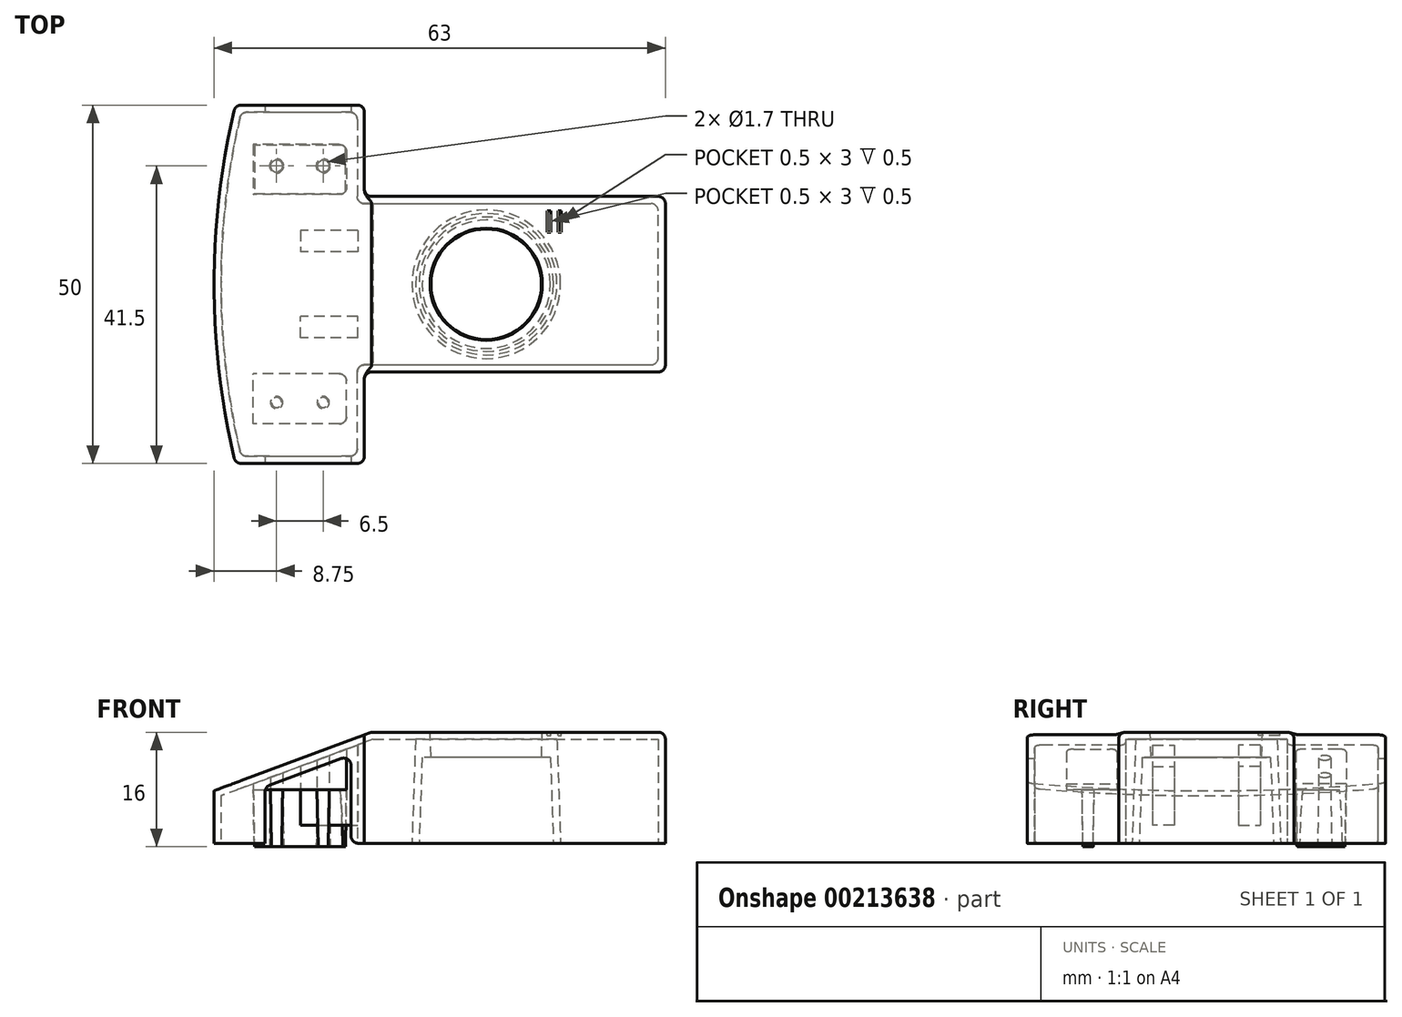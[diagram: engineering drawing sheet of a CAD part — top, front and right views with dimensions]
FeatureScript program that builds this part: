
annotation { "Feature Type Name" : "Feature", "Feature Type Description" : "" }
export const myFeature = defineFeature(function(context is Context, id is Id, definition is map)
    precondition{}
    {
        {
            var Q0;
            Q0=qCreatedBy(makeId("Top.planeOp"),FACE);
            var sketch = newSketch(context, id + "F0", { "sketchPlane" : qUnion([Q0])});
            skCircle(sketch, "E0", {"center": v(-4, 0) * mm, "radius": 9.37 * mm});
            skLineSegment(sketch, "E1.bottom", {"start": v(-21, -12.25) * mm, "end": v(21, -12.25) * mm});
            skLineSegment(sketch, "E1.top", {"start": v(-21, 12.25) * mm, "end": v(21, 12.25) * mm});
            skLineSegment(sketch, "E1.right", {"start": v(21, -12.25) * mm, "end": v(21, 12.25) * mm});
            skLineSegment(sketch, "E2.bottom", {"start": v(-21, -25) * mm, "end": v(-39, -25) * mm});
            skLineSegment(sketch, "E2.top", {"start": v(-21, 25) * mm, "end": v(-39, 25) * mm});
            skLineSegment(sketch, "E2.left", {"start": v(-21, -25) * mm, "end": v(-21, -12.25) * mm});
            skLineSegment(sketch, "E2.right", {"start": v(-39, -25) * mm, "end": v(-39, 25) * mm});
            skPoint(sketch, "E2.middle", {"position": v(-30, 0) * mm});
            skLineSegment(sketch, "E3.trimOffspring", {"start": v(-21, 12.25) * mm, "end": v(-21, 25) * mm});
            skLineSegment(sketch, "E4", {"start": v(-20, 12.25) * mm, "end": v(-20, -12.25) * mm});
            skPoint(sketch, "E5", {"position": v(-42, 0) * mm});
            skPoint(sketch, "E5.positionSnap0", {"position": v(-39, 0) * mm});
            skArc(sketch, "E6", {"start": v(-39, 25) * mm, "mid": v(-42, 0) * mm, "end": v(-39, -25) * mm});
            skSolve(sketch);
        }
        {
            var Q0;
            Q0=qSketchRegion(id+"F0",true);
            var Q1;
            Q1=makeQuery(id+"F0.imprint","IMPRINT",FACE,{"disambiguationData":[TD([[makeQuery(id+"F0.imprint","IMPRINT",EDGE,{"derivedFrom":sQuery(id+"F0.wireOp",EDGE,"E0")}),1.0]])]});
            extrude(context, id + "F1", {"entities" : qUnion([Q0, Q1]), "depth" : 15.5 * mm});
        }
        {
            var Q0;
            Q0=makeQuery(id+"F0.imprint","IMPRINT",FACE,{"disambiguationData":[TD([[makeQuery(id+"F0.imprint","IMPRINT",EDGE,{"derivedFrom":sQuery(id+"F0.wireOp",EDGE,"E0")}),1.0]])]});
            var Q1;
            Q1=makeQuery(id+"F1.opExtrude","CAP_FACE",FACE,{"disambiguationData":[OSD([sQuery(id+"F0.wireOp",EDGE,"E1.bottom"),sQuery(id+"F0.wireOp",EDGE,"E1.top"),sQuery(id+"F0.wireOp",EDGE,"E1.right"),sQuery(id+"F0.wireOp",EDGE,"E2.bottom"),sQuery(id+"F0.wireOp",EDGE,"E2.top"),sQuery(id+"F0.wireOp",EDGE,"E2.left"),sQuery(id+"F0.wireOp",EDGE,"E3.trimOffspring"),sQuery(id+"F0.wireOp",EDGE,"E6")])],"isStart":false});
            extrude(context, id + "F2", {"entities" : qUnion([Q0]), "operationType" : NewBodyOperationType.REMOVE, "endBound" : BoundingType.UP_TO_SURFACE, "endBoundEntityFace" : qUnion([Q1]), "depth" : 25 * mm, "hasDraft" : true, "draftAngle" : 2 * degree, "draftPullDirection" : true});
        }
        {
            var Q0;
            Q0=qCreatedBy(makeId("Front.planeOp"),FACE);
            var Q1;
            Q1=makeQuery(id+"F1.opExtrude","CAP_EDGE",EDGE,{"disambiguationData":[OSD([sQuery(id+"F0.wireOp",EDGE,"E2.bottom")])],"isStart":true});
            cPlane(context, id + "F3", {"entities" : qUnion([Q0, Q1]), "cplaneType" : CPlaneType.LINE_ANGLE, "offset" : 25 * mm, "angle" : 0 * degree, "width" : 150 * mm, "height" : 150 * mm});
        }
        {
            var Q0;
            Q0=qCreatedBy(id+"F3.planeOp",FACE);
            var sketch = newSketch(context, id + "F4", { "sketchPlane" : qUnion([Q0])});
            skLineSegment(sketch, "E7", {"start": v(20, 15.5) * mm, "end": v(42, 15.5) * mm});
            skLineSegment(sketch, "E8", {"start": v(42, 15.5) * mm, "end": v(42, 7.32) * mm});
            skLineSegment(sketch, "E9", {"start": v(42, 7.32) * mm, "end": v(20, 15.5) * mm});
            skLineSegment(sketch, "E10", {"start": v(42, 0) * mm, "end": v(41.46, 15.5) * mm, "construction": true});
            skLineSegment(sketch, "E11", {"start": v(42, 0) * mm, "end": v(42, 27.73) * mm, "construction": true});
            skSolve(sketch);
        }
        {
            var Q0;
            Q0=qSketchRegion(id+"F4",true);
            extrude(context, id + "F5", {"entities" : qUnion([Q0]), "operationType" : NewBodyOperationType.REMOVE, "endBound" : BoundingType.THROUGH_ALL, "depth" : 25 * mm});
        }
        {
            var Q0;
            Q0=makeQuery(id+"F1.opExtrude","CAP_FACE",FACE,{"disambiguationData":[OSD([sQuery(id+"F0.wireOp",EDGE,"E1.bottom"),sQuery(id+"F0.wireOp",EDGE,"E1.top"),sQuery(id+"F0.wireOp",EDGE,"E1.right"),sQuery(id+"F0.wireOp",EDGE,"E2.bottom"),sQuery(id+"F0.wireOp",EDGE,"E2.top"),sQuery(id+"F0.wireOp",EDGE,"E2.left"),sQuery(id+"F0.wireOp",EDGE,"E3.trimOffspring"),sQuery(id+"F0.wireOp",EDGE,"E6")])],"isStart":true});
            shell(context, id + "F6", {"entities" : qUnion([Q0]), "thickness" : 1 * mm});
        }
        {
            var Q0;
            Q0=makeQuery(id+"F1.opExtrude","SWEPT_FACE",FACE,{"disambiguationData":[OSD([sQuery(id+"F0.wireOp",EDGE,"E2.bottom")])]});
            var sketch = newSketch(context, id + "F7", { "sketchPlane" : qUnion([Q0])});
            skLineSegment(sketch, "E12", {"start": v(-20, 15.5) * mm, "end": v(-39, 8.43) * mm});
            skLineSegment(sketch, "E13", {"start": v(-39, 8.43) * mm, "end": v(-39, 15.5) * mm});
            skLineSegment(sketch, "E14", {"start": v(-39, 15.5) * mm, "end": v(-20, 15.5) * mm});
            skLineSegment(sketch, "E15", {"start": v(-34.87, 0) * mm, "end": v(-34.87, 7.86) * mm});
            skLineSegment(sketch, "E16", {"start": v(-34.87, 7.86) * mm, "end": v(-22.87, 12.32) * mm});
            skLineSegment(sketch, "E17", {"start": v(-22.87, 0) * mm, "end": v(-34.87, 0) * mm});
            skLineSegment(sketch, "E18", {"start": v(-22.87, 12.32) * mm, "end": v(-22.87, 0) * mm});
            skSolve(sketch);
        }
        {
            var Q0;
            Q0=makeQuery(id+"F7.imprint","IMPRINT",FACE,{"disambiguationData":[TD([[makeQuery(id+"F7.imprint","IMPRINT",EDGE,{"derivedFrom":sQuery(id+"F7.wireOp",EDGE,"E15")}),-1.0]])]});
            extrude(context, id + "F8", {"entities" : qUnion([Q0]), "operationType" : NewBodyOperationType.REMOVE, "endBound" : BoundingType.THROUGH_ALL, "oppositeDirection" : true, "depth" : 25 * mm});
        }
        {
            var Q0;
            Q0=makeQuery(id+"F1.opExtrude","CAP_FACE",FACE,{"disambiguationData":[OSD([sQuery(id+"F0.wireOp",EDGE,"E0"),sQuery(id+"F0.wireOp",EDGE,"E1.bottom"),sQuery(id+"F0.wireOp",EDGE,"E1.top"),sQuery(id+"F0.wireOp",EDGE,"E1.right"),sQuery(id+"F0.wireOp",EDGE,"E2.bottom"),sQuery(id+"F0.wireOp",EDGE,"E2.top"),sQuery(id+"F0.wireOp",EDGE,"E2.left"),sQuery(id+"F0.wireOp",EDGE,"E2.right"),sQuery(id+"F0.wireOp",EDGE,"E3.trimOffspring")])],"isStart":false});
            cPlane(context, id + "F9", {"entities" : qUnion([Q0]), "cplaneType" : CPlaneType.OFFSET, "offset" : 8 * mm, "oppositeDirection" : true, "width" : 150 * mm, "height" : 150 * mm});
        }
        {
            var Q0;
            Q0=qCreatedBy(id+"F9.planeOp",FACE);
            var sketch = newSketch(context, id + "F10", { "sketchPlane" : qUnion([Q0])});
            skLineSegment(sketch, "E19", {"start": v(0, 0) * mm, "end": v(-63, 0) * mm, "construction": true});
            skLineSegment(sketch, "E20.bottom", {"start": v(-36.5, -12.5) * mm, "end": v(-23.5, -12.5) * mm});
            skLineSegment(sketch, "E20.top", {"start": v(-36.5, -19.5) * mm, "end": v(-23.5, -19.5) * mm});
            skLineSegment(sketch, "E20.left", {"start": v(-36.5, -12.5) * mm, "end": v(-36.5, -19.5) * mm});
            skLineSegment(sketch, "E20.right", {"start": v(-23.5, -12.5) * mm, "end": v(-23.5, -19.5) * mm});
            skPoint(sketch, "E20.middle", {"position": v(-30, -16) * mm});
            skPoint(sketch, "E21", {"position": v(-33.25, -16.5) * mm});
            skPoint(sketch, "E22", {"position": v(-26.75, -16.5) * mm});
            skCircle(sketch, "E23", {"center": v(-33.25, -16.5) * mm, "radius": 0.85 * mm});
            skCircle(sketch, "E24", {"center": v(-26.75, -16.5) * mm, "radius": 0.85 * mm});
            skLineSegment(sketch, "E25.MirrorCS", {"start": v(-36.5, 12.5) * mm, "end": v(-23.5, 12.5) * mm});
            skLineSegment(sketch, "E26.MirrorCS", {"start": v(-36.5, 12.5) * mm, "end": v(-36.5, 19.5) * mm});
            skLineSegment(sketch, "E27.MirrorCS", {"start": v(-36.5, 19.5) * mm, "end": v(-23.5, 19.5) * mm});
            skLineSegment(sketch, "E28.MirrorCS", {"start": v(-23.5, 12.5) * mm, "end": v(-23.5, 19.5) * mm});
            skCircle(sketch, "E29.MirrorC", {"center": v(-26.75, 16.5) * mm, "radius": 0.85 * mm});
            skCircle(sketch, "E30.MirrorC", {"center": v(-33.25, 16.5) * mm, "radius": 0.85 * mm});
            skSolve(sketch);
        }
        {
            var Q0;
            Q0=makeQuery(id+"F10.imprint","IMPRINT",FACE,{"disambiguationData":[TD([[makeQuery(id+"F10.imprint","IMPRINT",EDGE,{"derivedFrom":sQuery(id+"F10.wireOp",EDGE,"E20.bottom")}),-1.0]])]});
            var Q1;
            Q1=makeQuery(id+"F10.imprint","IMPRINT",FACE,{"disambiguationData":[TD([[makeQuery(id+"F10.imprint","IMPRINT",EDGE,{"derivedFrom":sQuery(id+"F10.wireOp",EDGE,"E23")}),1.0]])]});
            var Q2;
            Q2=makeQuery(id+"F10.imprint","IMPRINT",FACE,{"disambiguationData":[TD([[makeQuery(id+"F10.imprint","IMPRINT",EDGE,{"derivedFrom":sQuery(id+"F10.wireOp",EDGE,"E24")}),1.0]])]});
            var Q3;
            Q3=makeQuery(id+"F10.imprint","IMPRINT",FACE,{"disambiguationData":[TD([[makeQuery(id+"F10.imprint","IMPRINT",EDGE,{"derivedFrom":sQuery(id+"F10.wireOp",EDGE,"E25.MirrorCS")}),1.0]])]});
            var Q4;
            Q4=makeQuery(id+"F10.imprint","IMPRINT",FACE,{"disambiguationData":[TD([[makeQuery(id+"F10.imprint","IMPRINT",EDGE,{"derivedFrom":sQuery(id+"F10.wireOp",EDGE,"E30.MirrorC")}),-1.0]])]});
            var Q5;
            Q5=makeQuery(id+"F10.imprint","IMPRINT",FACE,{"disambiguationData":[TD([[makeQuery(id+"F10.imprint","IMPRINT",EDGE,{"derivedFrom":sQuery(id+"F10.wireOp",EDGE,"E29.MirrorC")}),-1.0]])]});
            var Q6;
            Q6=makeQuery(id+"F6.opShell","OFFSET_FACE",FACE,{"disambiguationData":[OSD([sQuery(id+"F4.wireOp",EDGE,"E9")])]});
            extrude(context, id + "F11", {"entities" : qUnion([Q0, Q1, Q2, Q3, Q4, Q5]), "operationType" : NewBodyOperationType.ADD, "endBound" : BoundingType.UP_TO_SURFACE, "endBoundEntityFace" : qUnion([Q6]), "depth" : 25 * mm});
        }
        {
            var Q0;
            Q0=makeQuery(id+"F10.imprint","IMPRINT",FACE,{"disambiguationData":[TD([[makeQuery(id+"F10.imprint","IMPRINT",EDGE,{"derivedFrom":sQuery(id+"F10.wireOp",EDGE,"E23")}),1.0]])]});
            var Q1;
            Q1=makeQuery(id+"F10.imprint","IMPRINT",FACE,{"disambiguationData":[TD([[makeQuery(id+"F10.imprint","IMPRINT",EDGE,{"derivedFrom":sQuery(id+"F10.wireOp",EDGE,"E29.MirrorC")}),-1.0]])]});
            var Q2;
            Q2=makeQuery(id+"F10.imprint","IMPRINT",FACE,{"disambiguationData":[TD([[makeQuery(id+"F10.imprint","IMPRINT",EDGE,{"derivedFrom":sQuery(id+"F10.wireOp",EDGE,"E30.MirrorC")}),-1.0]])]});
            var Q3;
            Q3=makeQuery(id+"F10.imprint","IMPRINT",FACE,{"disambiguationData":[TD([[makeQuery(id+"F10.imprint","IMPRINT",EDGE,{"derivedFrom":sQuery(id+"F10.wireOp",EDGE,"E24")}),1.0]])]});
            extrude(context, id + "F12", {"entities" : qUnion([Q0, Q1, Q2, Q3]), "operationType" : NewBodyOperationType.ADD, "oppositeDirection" : true, "depth" : 8 * mm, "hasDraft" : true, "draftAngle" : 1 * degree, "draftPullDirection" : true});
        }
        {
            var Q0;
            Q0=makeQuery(id+"F1.opExtrude","CAP_EDGE",EDGE,{"disambiguationData":[OSD([sQuery(id+"F0.wireOp",EDGE,"E1.bottom")])],"isStart":false});
            var Q1;
            Q1=makeQuery(id+"F1.opExtrude","CAP_EDGE",EDGE,{"disambiguationData":[OSD([sQuery(id+"F0.wireOp",EDGE,"E1.right")])],"isStart":false});
            var Q2;
            Q2=makeQuery(id+"F1.opExtrude","CAP_EDGE",EDGE,{"disambiguationData":[OSD([sQuery(id+"F0.wireOp",EDGE,"E1.top")])],"isStart":false});
            var Q3;
            Q3=makeQuery(id+"F1.opExtrude","SWEPT_EDGE",EDGE,{"disambiguationData":[OSD([sQuery(id+"F0.wireOp",EDGE,"E1.bottom"),sQuery(id+"F0.wireOp",EDGE,"E1.right")])]});
            var Q4;
            Q4=makeQuery(id+"F1.opExtrude","SWEPT_EDGE",EDGE,{"disambiguationData":[OSD([sQuery(id+"F0.wireOp",EDGE,"E1.top"),sQuery(id+"F0.wireOp",EDGE,"E1.right")])]});
            fillet(context, id + "F13", {"entities" : qUnion([Q0, Q1, Q2, Q3, Q4]), "radius" : 1 * mm, "tangentPropagation" : true, "allowEdgeOverflow" : false});
        }
        {
            var Q0;
            Q0=makeQuery(id+"F1.opExtrude","SWEPT_EDGE",EDGE,{"disambiguationData":[OSD([sQuery(id+"F0.wireOp",EDGE,"E2.bottom"),sQuery(id+"F0.wireOp",EDGE,"E2.left")])]});
            var Q1;
            Q1=makeQuery(id+"F5.boolean.opBoolean","INTERSECT",EDGE,{"derivedFrom":[makeQuery(id+"F1.opExtrude","SWEPT_FACE",FACE,{"disambiguationData":[OSD([sQuery(id+"F0.wireOp",EDGE,"E2.left")])]}),makeQuery(id+"F5.opExtrude","SWEPT_FACE",FACE,{"disambiguationData":[OSD([sQuery(id+"FjstzwEYRuGCUyq_1.wireOp",EDGE,"6156deb2-2619-4c56-9df6-34b3699534c4")])]})]});
            var Q2;
            Q2=makeQuery(id+"F5.boolean.opBoolean","COPY",EDGE,{"derivedFrom":makeQuery(id+"F5.opExtrude","CAP_EDGE",EDGE,{"disambiguationData":[OSD([sQuery(id+"FjstzwEYRuGCUyq_1.wireOp",EDGE,"6156deb2-2619-4c56-9df6-34b3699534c4")])],"isStart":true})});
            var Q3;
            Q3=makeQuery(id+"F1.opExtrude","SWEPT_EDGE",EDGE,{"disambiguationData":[OSD([sQuery(id+"F0.wireOp",EDGE,"E2.bottom"),sQuery(id+"F0.wireOp",EDGE,"E2.right"),sQuery(id+"F0.wireOp",EDGE,"E6")])]});
            var Q4;
            Q4=makeQuery(id+"F5.boolean.opBoolean","INTERSECT",EDGE,{"derivedFrom":[makeQuery(id+"F1.opExtrude","SWEPT_FACE",FACE,{"disambiguationData":[OSD([sQuery(id+"F0.wireOp",EDGE,"E6")])]}),makeQuery(id+"F5.opExtrude","SWEPT_FACE",FACE,{"disambiguationData":[OSD([sQuery(id+"FjstzwEYRuGCUyq_1.wireOp",EDGE,"6156deb2-2619-4c56-9df6-34b3699534c4")])]})]});
            var Q5;
            Q5=makeQuery(id+"F5.boolean.opBoolean","INTERSECT",EDGE,{"derivedFrom":[makeQuery(id+"F1.opExtrude","SWEPT_FACE",FACE,{"disambiguationData":[OSD([sQuery(id+"F0.wireOp",EDGE,"E2.top")])]}),makeQuery(id+"F5.opExtrude","SWEPT_FACE",FACE,{"disambiguationData":[OSD([sQuery(id+"FjstzwEYRuGCUyq_1.wireOp",EDGE,"6156deb2-2619-4c56-9df6-34b3699534c4")])]})]});
            var Q6;
            Q6=makeQuery(id+"F1.opExtrude","SWEPT_EDGE",EDGE,{"disambiguationData":[OSD([sQuery(id+"F0.wireOp",EDGE,"E2.top"),sQuery(id+"F0.wireOp",EDGE,"E2.right"),sQuery(id+"F0.wireOp",EDGE,"E6")])]});
            var Q7;
            Q7=makeQuery(id+"F1.opExtrude","SWEPT_EDGE",EDGE,{"disambiguationData":[OSD([sQuery(id+"F0.wireOp",EDGE,"E2.top"),sQuery(id+"F0.wireOp",EDGE,"E3.trimOffspring")])]});
            var Q8;
            Q8=makeQuery(id+"F5.boolean.opBoolean","INTERSECT",EDGE,{"derivedFrom":[makeQuery(id+"F1.opExtrude","SWEPT_FACE",FACE,{"disambiguationData":[OSD([sQuery(id+"F0.wireOp",EDGE,"E3.trimOffspring")])]}),makeQuery(id+"F5.opExtrude","SWEPT_FACE",FACE,{"disambiguationData":[OSD([sQuery(id+"FjstzwEYRuGCUyq_1.wireOp",EDGE,"6156deb2-2619-4c56-9df6-34b3699534c4")])]})]});
            fillet(context, id + "F14", {"entities" : qUnion([Q0, Q1, Q2, Q3, Q4, Q5, Q6, Q7, Q8]), "radius" : 1 * mm, "tangentPropagation" : true, "allowEdgeOverflow" : false});
        }
        {
            var Q0;
            Q0=makeQuery(id+"F1.opExtrude","SWEPT_EDGE",EDGE,{"disambiguationData":[OSD([sQuery(id+"F0.wireOp",EDGE,"E1.top"),sQuery(id+"F0.wireOp",EDGE,"E3.trimOffspring")])]});
            fillet(context, id + "F15", {"entities" : qUnion([Q0]), "radius" : 1 * mm, "tangentPropagation" : true, "allowEdgeOverflow" : false});
        }
        {
            var Q0;
            Q0=makeQuery(id+"F1.opExtrude","SWEPT_EDGE",EDGE,{"disambiguationData":[OSD([sQuery(id+"F0.wireOp",EDGE,"E1.bottom"),sQuery(id+"F0.wireOp",EDGE,"E2.left")])]});
            var Q1;
            {var subQ0=sQuery(id+"F0.wireOp",EDGE,"E2.bottom");var subQ1=sQuery(id+"F7.wireOp",EDGE,"E18");Q1=makeQuery(id+"F8.boolean.opBoolean","COPY",EDGE,{"disambiguationData":[TD([makeQuery(id+"F1.opExtrude","SWEPT_FACE",FACE,{"disambiguationData":[OSD([subQ0])]})])],"derivedFrom":makeQuery(id+"F8.opExtrude","SWEPT_EDGE",EDGE,{"disambiguationData":[OSD([subQ0,sQuery(id+"F7.wireOp",EDGE,"E17"),subQ1])]})});}
            var Q2;
            {var subQ0=sQuery(id+"F0.wireOp",EDGE,"E2.bottom");var subQ1=sQuery(id+"F7.wireOp",EDGE,"E15");Q2=makeQuery(id+"F8.boolean.opBoolean","COPY",EDGE,{"disambiguationData":[TD([makeQuery(id+"F1.opExtrude","SWEPT_FACE",FACE,{"disambiguationData":[OSD([subQ0])]})])],"derivedFrom":makeQuery(id+"F8.opExtrude","SWEPT_EDGE",EDGE,{"disambiguationData":[OSD([subQ0,subQ1,sQuery(id+"F7.wireOp",EDGE,"E17")])]})});}
            var Q3;
            {var subQ0=sQuery(id+"F0.wireOp",EDGE,"E2.top");var subQ1=sQuery(id+"F0.wireOp",EDGE,"E2.bottom");var subQ2=sQuery(id+"F7.wireOp",EDGE,"E15");Q3=makeQuery(id+"F8.boolean.opBoolean","COPY",EDGE,{"disambiguationData":[TD([makeQuery(id+"F1.opExtrude","SWEPT_FACE",FACE,{"disambiguationData":[OSD([subQ0])]})])],"derivedFrom":makeQuery(id+"F8.opExtrude","SWEPT_EDGE",EDGE,{"disambiguationData":[OSD([subQ1,subQ2,sQuery(id+"F7.wireOp",EDGE,"E17")])]})});}
            var Q4;
            {var subQ0=sQuery(id+"F0.wireOp",EDGE,"E2.top");var subQ1=sQuery(id+"F0.wireOp",EDGE,"E2.bottom");var subQ2=sQuery(id+"F7.wireOp",EDGE,"E18");Q4=makeQuery(id+"F8.boolean.opBoolean","COPY",EDGE,{"disambiguationData":[TD([makeQuery(id+"F1.opExtrude","SWEPT_FACE",FACE,{"disambiguationData":[OSD([subQ0])]})])],"derivedFrom":makeQuery(id+"F8.opExtrude","SWEPT_EDGE",EDGE,{"disambiguationData":[OSD([subQ1,sQuery(id+"F7.wireOp",EDGE,"E17"),subQ2])]})});}
            var Q5;
            {var subQ0=sQuery(id+"F0.wireOp",EDGE,"E2.top");var subQ1=sQuery(id+"F7.wireOp",EDGE,"E18");var subQ2=sQuery(id+"F7.wireOp",EDGE,"E16");Q5=makeQuery(id+"F8.boolean.opBoolean","COPY",EDGE,{"disambiguationData":[TD([makeQuery(id+"F1.opExtrude","SWEPT_FACE",FACE,{"disambiguationData":[OSD([subQ0])]})])],"derivedFrom":makeQuery(id+"F8.opExtrude","SWEPT_EDGE",EDGE,{"disambiguationData":[OSD([subQ2,subQ1])]})});}
            var Q6;
            {var subQ0=sQuery(id+"F0.wireOp",EDGE,"E2.top");var subQ1=sQuery(id+"F7.wireOp",EDGE,"E15");var subQ2=sQuery(id+"F7.wireOp",EDGE,"E16");Q6=makeQuery(id+"F8.boolean.opBoolean","COPY",EDGE,{"disambiguationData":[TD([makeQuery(id+"F1.opExtrude","SWEPT_FACE",FACE,{"disambiguationData":[OSD([subQ0])]})])],"derivedFrom":makeQuery(id+"F8.opExtrude","SWEPT_EDGE",EDGE,{"disambiguationData":[OSD([subQ1,subQ2])]})});}
            var Q7;
            {var subQ0=sQuery(id+"F0.wireOp",EDGE,"E2.bottom");var subQ1=sQuery(id+"F7.wireOp",EDGE,"E18");var subQ2=sQuery(id+"F7.wireOp",EDGE,"E16");Q7=makeQuery(id+"F8.boolean.opBoolean","COPY",EDGE,{"disambiguationData":[TD([makeQuery(id+"F1.opExtrude","SWEPT_FACE",FACE,{"disambiguationData":[OSD([subQ0])]})])],"derivedFrom":makeQuery(id+"F8.opExtrude","SWEPT_EDGE",EDGE,{"disambiguationData":[OSD([subQ2,subQ1])]})});}
            var Q8;
            {var subQ0=sQuery(id+"F0.wireOp",EDGE,"E2.bottom");var subQ1=sQuery(id+"F7.wireOp",EDGE,"E15");var subQ2=sQuery(id+"F7.wireOp",EDGE,"E16");Q8=makeQuery(id+"F8.boolean.opBoolean","COPY",EDGE,{"disambiguationData":[TD([makeQuery(id+"F1.opExtrude","SWEPT_FACE",FACE,{"disambiguationData":[OSD([subQ0])]})])],"derivedFrom":makeQuery(id+"F8.opExtrude","SWEPT_EDGE",EDGE,{"disambiguationData":[OSD([subQ1,subQ2])]})});}
            var Q9;
            Q9=makeQuery(id+"F6.opShell","OFFSET_EDGE",EDGE,{"disambiguationData":[OSD([sQuery(id+"F0.wireOp",EDGE,"E1.top"),sQuery(id+"F0.wireOp",EDGE,"E3.trimOffspring")])]});
            var Q10;
            Q10=makeQuery(id+"F6.opShell","OFFSET_EDGE",EDGE,{"disambiguationData":[OSD([sQuery(id+"F0.wireOp",EDGE,"E1.bottom"),sQuery(id+"F0.wireOp",EDGE,"E2.left")])]});
            fillet(context, id + "F16", {"entities" : qUnion([Q0, Q1, Q2, Q3, Q4, Q5, Q6, Q7, Q8, Q9, Q10]), "radius" : 1 * mm, "tangentPropagation" : true, "allowEdgeOverflow" : false});
        }
        {
            var Q0;
            Q0=makeQuery(id+"F6.opShell","OFFSET_EDGE",EDGE,{"disambiguationData":[OSD([sQuery(id+"F0.wireOp",EDGE,"E1.top"),sQuery(id+"F0.wireOp",EDGE,"E1.right")])]});
            var Q1;
            Q1=makeQuery(id+"F6.opShell","OFFSET_EDGE",EDGE,{"disambiguationData":[OSD([sQuery(id+"F0.wireOp",EDGE,"E1.bottom"),sQuery(id+"F0.wireOp",EDGE,"E1.right")])]});
            var Q2;
            {var subQ0=sQuery(id+"F0.wireOp",EDGE,"E0");Q2=makeQuery(id+"F6.opShell","OFFSET_EDGE",EDGE,{"disambiguationData":[OSD([subQ0]),TDD([makeQuery(id+"F1.opExtrude","CAP_EDGE",EDGE,{"disambiguationData":[OSD([subQ0])],"isStart":false})])]});}
            var Q3;
            Q3=makeQuery(id+"F6.opShell","OFFSET_EDGE",EDGE,{"disambiguationData":[OSD([sQuery(id+"F0.wireOp",EDGE,"E2.top"),sQuery(id+"F0.wireOp",EDGE,"E3.trimOffspring")])]});
            var Q4;
            Q4=makeQuery(id+"F6.opShell","OFFSET_EDGE",EDGE,{"disambiguationData":[OSD([sQuery(id+"F0.wireOp",EDGE,"E2.top"),sQuery(id+"F0.wireOp",EDGE,"E2.right"),sQuery(id+"F0.wireOp",EDGE,"E6")])]});
            var Q5;
            Q5=makeQuery(id+"F6.opShell","OFFSET_EDGE",EDGE,{"disambiguationData":[OSD([sQuery(id+"F0.wireOp",EDGE,"E2.bottom"),sQuery(id+"F0.wireOp",EDGE,"E2.left")])]});
            var Q6;
            Q6=makeQuery(id+"F6.opShell","OFFSET_EDGE",EDGE,{"disambiguationData":[OSD([sQuery(id+"F0.wireOp",EDGE,"E2.bottom"),sQuery(id+"F0.wireOp",EDGE,"E2.right"),sQuery(id+"F0.wireOp",EDGE,"E6")])]});
            var Q7;
            Q7=makeQuery(id+"F11.opExtrude","SWEPT_EDGE",EDGE,{"disambiguationData":[OSD([sQuery(id+"F10.wireOp",EDGE,"E20.bottom"),sQuery(id+"F10.wireOp",EDGE,"E20.right")])]});
            var Q8;
            Q8=makeQuery(id+"F11.opExtrude","SWEPT_EDGE",EDGE,{"disambiguationData":[OSD([sQuery(id+"F10.wireOp",EDGE,"E20.top"),sQuery(id+"F10.wireOp",EDGE,"E20.right")])]});
            var Q9;
            Q9=makeQuery(id+"F11.opExtrude","SWEPT_EDGE",EDGE,{"disambiguationData":[OSD([sQuery(id+"F10.wireOp",EDGE,"E27.MirrorCS"),sQuery(id+"F10.wireOp",EDGE,"E28.MirrorCS")])]});
            var Q10;
            Q10=makeQuery(id+"F11.opExtrude","SWEPT_EDGE",EDGE,{"disambiguationData":[OSD([sQuery(id+"F10.wireOp",EDGE,"E25.MirrorCS"),sQuery(id+"F10.wireOp",EDGE,"E28.MirrorCS")])]});
            fillet(context, id + "F17", {"entities" : qUnion([Q0, Q1, Q2, Q3, Q4, Q5, Q6, Q7, Q8, Q9, Q10]), "radius" : 1 * mm, "tangentPropagation" : true, "allowEdgeOverflow" : false});
        }
        {
            var Q0;
            Q0=qCreatedBy(id+"F9.planeOp",FACE);
            var sketch = newSketch(context, id + "F18", { "sketchPlane" : qUnion([Q0])});
            skPoint(sketch, "E31", {"position": v(-29.94, -4.5) * mm});
            skLineSegment(sketch, "E32.bottom", {"start": v(-29.94, -4.5) * mm, "end": v(-21.94, -4.5) * mm});
            skLineSegment(sketch, "E32.top", {"start": v(-29.94, -7.5) * mm, "end": v(-21.94, -7.5) * mm});
            skLineSegment(sketch, "E32.left", {"start": v(-29.94, -4.5) * mm, "end": v(-29.94, -7.5) * mm});
            skLineSegment(sketch, "E32.right", {"start": v(-21.94, -4.5) * mm, "end": v(-21.94, -7.5) * mm});
            skLineSegment(sketch, "E33", {"start": v(0, 0) * mm, "end": v(-48.4, 0) * mm, "construction": true});
            skLineSegment(sketch, "E34.MirrorCS", {"start": v(-29.94, 4.5) * mm, "end": v(-21.94, 4.5) * mm});
            skLineSegment(sketch, "E35.MirrorCS", {"start": v(-21.94, 4.5) * mm, "end": v(-21.94, 7.5) * mm});
            skLineSegment(sketch, "E36.MirrorCS", {"start": v(-29.94, 7.5) * mm, "end": v(-21.94, 7.5) * mm});
            skLineSegment(sketch, "E37.MirrorCS", {"start": v(-29.94, 4.5) * mm, "end": v(-29.94, 7.5) * mm});
            skSolve(sketch);
        }
        {
            var Q0;
            Q0=qSketchRegion(id+"F18",true);
            var Q1;
            Q1=makeQuery(id+"F6.opShell","OFFSET_FACE",FACE,{"disambiguationData":[OSD([sQuery(id+"F4.wireOp",EDGE,"E9")])]});
            extrude(context, id + "F19", {"entities" : qUnion([Q0]), "operationType" : NewBodyOperationType.ADD, "endBound" : BoundingType.UP_TO_SURFACE, "endBoundEntityFace" : qUnion([Q1]), "depth" : 25 * mm, "hasSecondDirection" : true, "secondDirectionOppositeDirection" : true, "secondDirectionDepth" : 5 * mm});
        }
        {
            var Q0;
            Q0=makeQuery(id+"F1.opExtrude","CAP_FACE",FACE,{"disambiguationData":[OSD([sQuery(id+"F0.wireOp",EDGE,"E1.bottom"),sQuery(id+"F0.wireOp",EDGE,"E1.top"),sQuery(id+"F0.wireOp",EDGE,"E1.right"),sQuery(id+"F0.wireOp",EDGE,"E2.bottom"),sQuery(id+"F0.wireOp",EDGE,"E2.top"),sQuery(id+"F0.wireOp",EDGE,"E2.left"),sQuery(id+"F0.wireOp",EDGE,"E3.trimOffspring"),sQuery(id+"F0.wireOp",EDGE,"E6")])],"isStart":false});
            var sketch = newSketch(context, id + "F20", { "sketchPlane" : qUnion([Q0])});
            skCircle(sketch, "E38", {"center": v(-4, 0) * mm, "radius": 8.83 * mm});
            skCircle(sketch, "E39.0", {"center": v(-4, 0) * mm, "radius": 7.83 * mm});
            skSolve(sketch);
        }
        {
            var Q0;
            Q0 = qSketchRegion(id + "F20", true);
            extrude(context, id + "F21", {"entities" : qUnion([Q0]), "operationType" : NewBodyOperationType.ADD, "oppositeDirection" : true, "depth" : 3.5 * mm, "hasDraft" : true, "draftAngle" : 2 * degree});
        }
        {
            var Q0;
            Q0=makeQuery(id+"F21.boolean.opBoolean","MERGE",FACE,{"derivedFrom":[makeQuery(id+"F1.opExtrude","CAP_FACE",FACE,{"disambiguationData":[OSD([sQuery(id+"F0.wireOp",EDGE,"E1.bottom"),sQuery(id+"F0.wireOp",EDGE,"E1.top"),sQuery(id+"F0.wireOp",EDGE,"E1.right"),sQuery(id+"F0.wireOp",EDGE,"E2.bottom"),sQuery(id+"F0.wireOp",EDGE,"E2.top"),sQuery(id+"F0.wireOp",EDGE,"E2.left"),sQuery(id+"F0.wireOp",EDGE,"E3.trimOffspring"),sQuery(id+"F0.wireOp",EDGE,"E6")])],"isStart":false}),makeQuery(id+"F21.opExtrude","CAP_FACE",FACE,{"disambiguationData":[OSD([sQuery(id+"F20.wireOp",EDGE,"E38"),sQuery(id+"F20.wireOp",EDGE,"E39.0")])],"isStart":true})]});
            var sketch = newSketch(context, id + "F22", { "sketchPlane" : qUnion([Q0])});
            skLineSegment(sketch, "E40.bottom", {"start": v(4.5, 10.25) * mm, "end": v(5, 10.25) * mm});
            skLineSegment(sketch, "E40.top", {"start": v(4.5, 7.25) * mm, "end": v(5, 7.25) * mm});
            skLineSegment(sketch, "E40.left", {"start": v(4.5, 10.25) * mm, "end": v(4.5, 7.25) * mm});
            skLineSegment(sketch, "E40.right", {"start": v(5, 10.25) * mm, "end": v(5, 7.25) * mm});
            skLineSegment(sketch, "E41.bottom", {"start": v(6, 10.25) * mm, "end": v(6.5, 10.25) * mm});
            skLineSegment(sketch, "E41.top", {"start": v(6, 7.25) * mm, "end": v(6.5, 7.25) * mm});
            skLineSegment(sketch, "E41.left", {"start": v(6, 10.25) * mm, "end": v(6, 7.25) * mm});
            skLineSegment(sketch, "E41.right", {"start": v(6.5, 10.25) * mm, "end": v(6.5, 7.25) * mm});
            skSolve(sketch);
        }
        {
            var Q0;
            Q0 = qSketchRegion(id + "F22", true);
            extrude(context, id + "F23", {"entities" : qUnion([Q0]), "operationType" : NewBodyOperationType.REMOVE, "oppositeDirection" : true, "depth" : 0.5 * mm});
        }
    });
